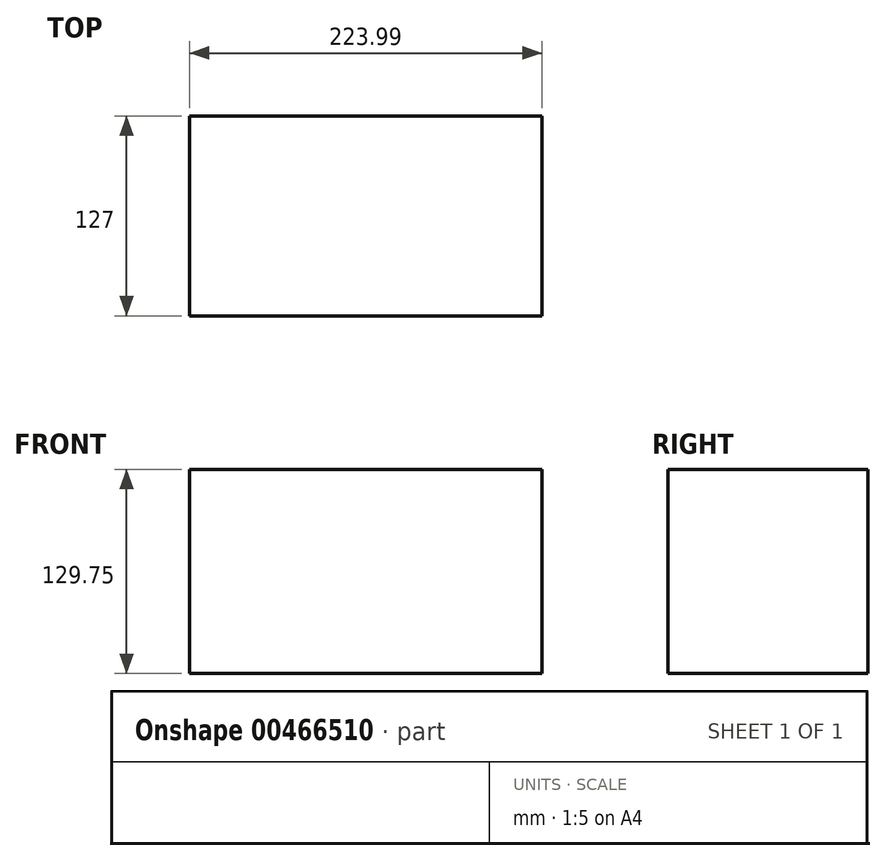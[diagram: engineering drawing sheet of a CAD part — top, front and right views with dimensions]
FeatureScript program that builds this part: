
annotation { "Feature Type Name" : "Feature", "Feature Type Description" : "" }
export const myFeature = defineFeature(function(context is Context, id is Id, definition is map)
    precondition{}
    {
        {
            var Q0;
            Q0=qCreatedBy(makeId("Front.planeOp"),FACE);
            var sketch = newSketch(context, id + "F0", { "sketchPlane" : qUnion([Q0])});
            skLineSegment(sketch, "E0.bottom", {"start": v(-149.54, 60.7) * mm, "end": v(74.45, 60.7) * mm});
            skLineSegment(sketch, "E0.top", {"start": v(-149.54, -69.05) * mm, "end": v(74.45, -69.05) * mm});
            skLineSegment(sketch, "E0.left", {"start": v(-149.54, 60.7) * mm, "end": v(-149.54, -69.05) * mm});
            skLineSegment(sketch, "E0.right", {"start": v(74.45, 60.7) * mm, "end": v(74.45, -69.05) * mm});
            skSolve(sketch);
        }
        {
            var Q0;
            Q0 = qSketchRegion(id + "F0", true);
            extrude(context, id + "F1", {"entities" : qUnion([Q0]), "depth" : 127 * mm});
        }
    });
